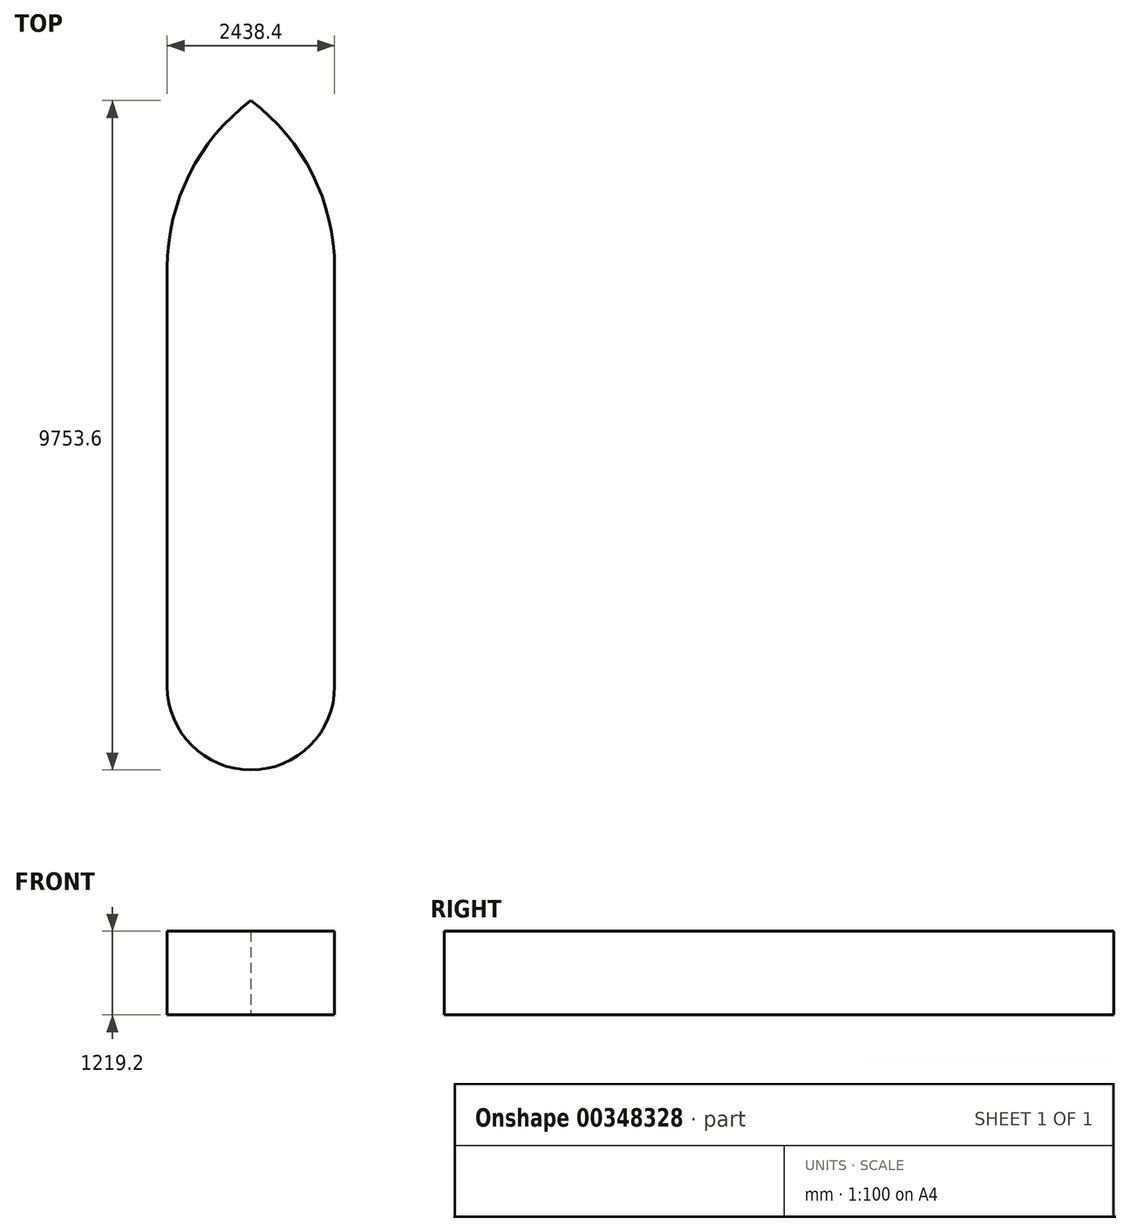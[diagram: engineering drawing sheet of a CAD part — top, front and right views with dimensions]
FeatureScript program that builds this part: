
annotation { "Feature Type Name" : "Feature", "Feature Type Description" : "" }
export const myFeature = defineFeature(function(context is Context, id is Id, definition is map)
    precondition{}
    {
        {
            var Q0;
            Q0=qCreatedBy(makeId("Top.planeOp"),FACE);
            var sketch = newSketch(context, id + "F0", { "sketchPlane" : qUnion([Q0])});
            skLineSegment(sketch, "E0", {"start": v(1219.2, -8534.4) * mm, "end": v(1219.2, -2438.4) * mm});
            skArc(sketch, "E1", {"start": v(1219.2, -2438.4) * mm, "mid": v(897.41, -1075.3) * mm, "end": v(0, 0) * mm});
            skLineSegment(sketch, "E2.MirrorCS", {"start": v(-1219.2, -8534.4) * mm, "end": v(-1219.2, -2438.4) * mm});
            skArc(sketch, "E3.MirrorCS", {"start": v(-1219.2, -2438.4) * mm, "mid": v(-897.41, -1075.3) * mm, "end": v(0, 0) * mm});
            skArc(sketch, "E4", {"start": v(-1219.2, -8534.4) * mm, "mid": v(0, -9753.6) * mm, "end": v(1219.2, -8534.4) * mm});
            skSolve(sketch);
        }
        {
            var Q0;
            Q0=makeQuery(id+"F0.imprint","IMPRINT",FACE,{"disambiguationData":[TD([[makeQuery(id+"F0.imprint","IMPRINT",EDGE,{"derivedFrom":sQuery(id+"F0.wireOp",EDGE,"E0")}),1.0]])]});
            extrude(context, id + "F1", {"entities" : qUnion([Q0]), "depth" : 1219.2 * mm});
        }
    });
